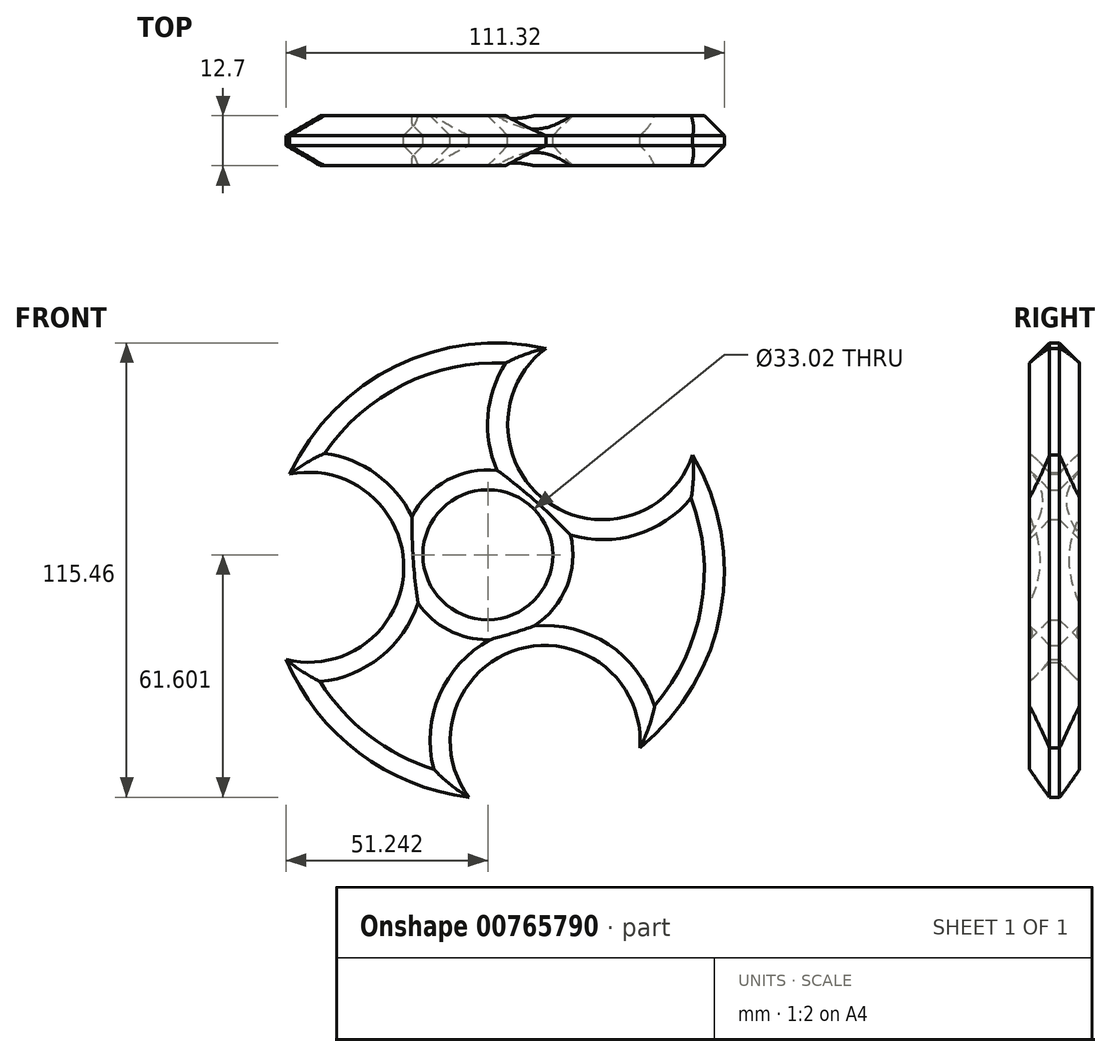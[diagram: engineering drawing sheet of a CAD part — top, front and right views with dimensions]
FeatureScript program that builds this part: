
annotation { "Feature Type Name" : "Feature", "Feature Type Description" : "" }
export const myFeature = defineFeature(function(context is Context, id is Id, definition is map)
    precondition{}
    {
        {
            var Q0;
            Q0=qCreatedBy(makeId("Front.planeOp"),FACE);
            var sketch = newSketch(context, id + "F0", { "sketchPlane" : qUnion([Q0])});
            skCircle(sketch, "E0", {"center": v(-72.8, -8.97) * mm, "radius": 57.94 * mm});
            skSolve(sketch);
        }
        {
            var Q0;
            Q0=qCreatedBy(makeId("Front.planeOp"),FACE);
            var sketch = newSketch(context, id + "F1", { "sketchPlane" : qUnion([Q0])});
            skPoint(sketch, "E1", {"position": v(-45.79, 28.15) * mm});
            skPoint(sketch, "E2", {"position": v(-120.44, -8.06) * mm});
            skPoint(sketch, "E3", {"position": v(-60.4, -52.07) * mm});
            skSolve(sketch);
        }
        {
            var Q0;
            Q0 = qSketchRegion(id + "F0", true);
            extrude(context, id + "F2", {"entities" : qUnion([Q0]), "depth" : 12.7 * mm, "offsetDistance" : 25.4 * mm});
        }
        {
            var Q0;
            Q0=sQuery(id+"F1.wireOp",VERTEX,"E1");
            var Q1;
            Q1=sQuery(id+"F1.wireOp",VERTEX,"E2");
            var Q2;
            Q2=sQuery(id+"F1.wireOp",VERTEX,"E3");
            var Q3;
            Q3=makeQuery(id+"F2.opExtrude","SWEPT_BODY",BODY,{"disambiguationData":[OSD([sQuery(id+"F0.wireOp",EDGE,"E0")])]});
            hole(context, id + "F3", {"style" : HoleStyle.SIMPLE, "endStyle" : HoleEndStyle.THROUGH, "oppositeDirection" : true, "holeDiameter" : 48.26 * mm, "majorDiameter" : 6.35 * mm, "isTappedThrough" : true, "tappedDepth" : 12.7 * mm, "tapClearance" : 3, "locations" : qUnion([Q0, Q1, Q2]), "scope" : qUnion([Q3])});
        }
        {
            var Q0;
            Q0=qCreatedBy(makeId("Front.planeOp"),FACE);
            var sketch = newSketch(context, id + "F4", { "sketchPlane" : qUnion([Q0])});
            skPoint(sketch, "E4", {"position": v(-74.94, -4.89) * mm});
            skSolve(sketch);
        }
        {
            var Q0;
            Q0=sQuery(id+"F4.wireOp",VERTEX,"E4");
            var Q1;
            Q1=makeQuery(id+"F2.opExtrude","SWEPT_BODY",BODY,{"disambiguationData":[OSD([sQuery(id+"F0.wireOp",EDGE,"E0")])]});
            hole(context, id + "F5", {"style" : HoleStyle.SIMPLE, "endStyle" : HoleEndStyle.THROUGH, "oppositeDirection" : true, "holeDiameter" : 33.02 * mm, "majorDiameter" : 6.35 * mm, "isTappedThrough" : true, "tappedDepth" : 12.7 * mm, "tapClearance" : 3, "locations" : qUnion([Q0]), "scope" : qUnion([Q1])});
        }
        {
            var Q0;
            Q0=makeQuery(id+"F2.opExtrude","CAP_FACE",FACE,{"disambiguationData":[OSD([sQuery(id+"F0.wireOp",EDGE,"E0")])],"isStart":false});
            var Q1;
            Q1=makeQuery(id+"F2.opExtrude","CAP_FACE",FACE,{"disambiguationData":[OSD([sQuery(id+"F0.wireOp",EDGE,"E0")])],"isStart":true});
            chamfer(context, id + "F6", {"entities" : qUnion([Q0, Q1]), "width" : 5.08 * mm, "tangentPropagation" : true});
        }
    });
